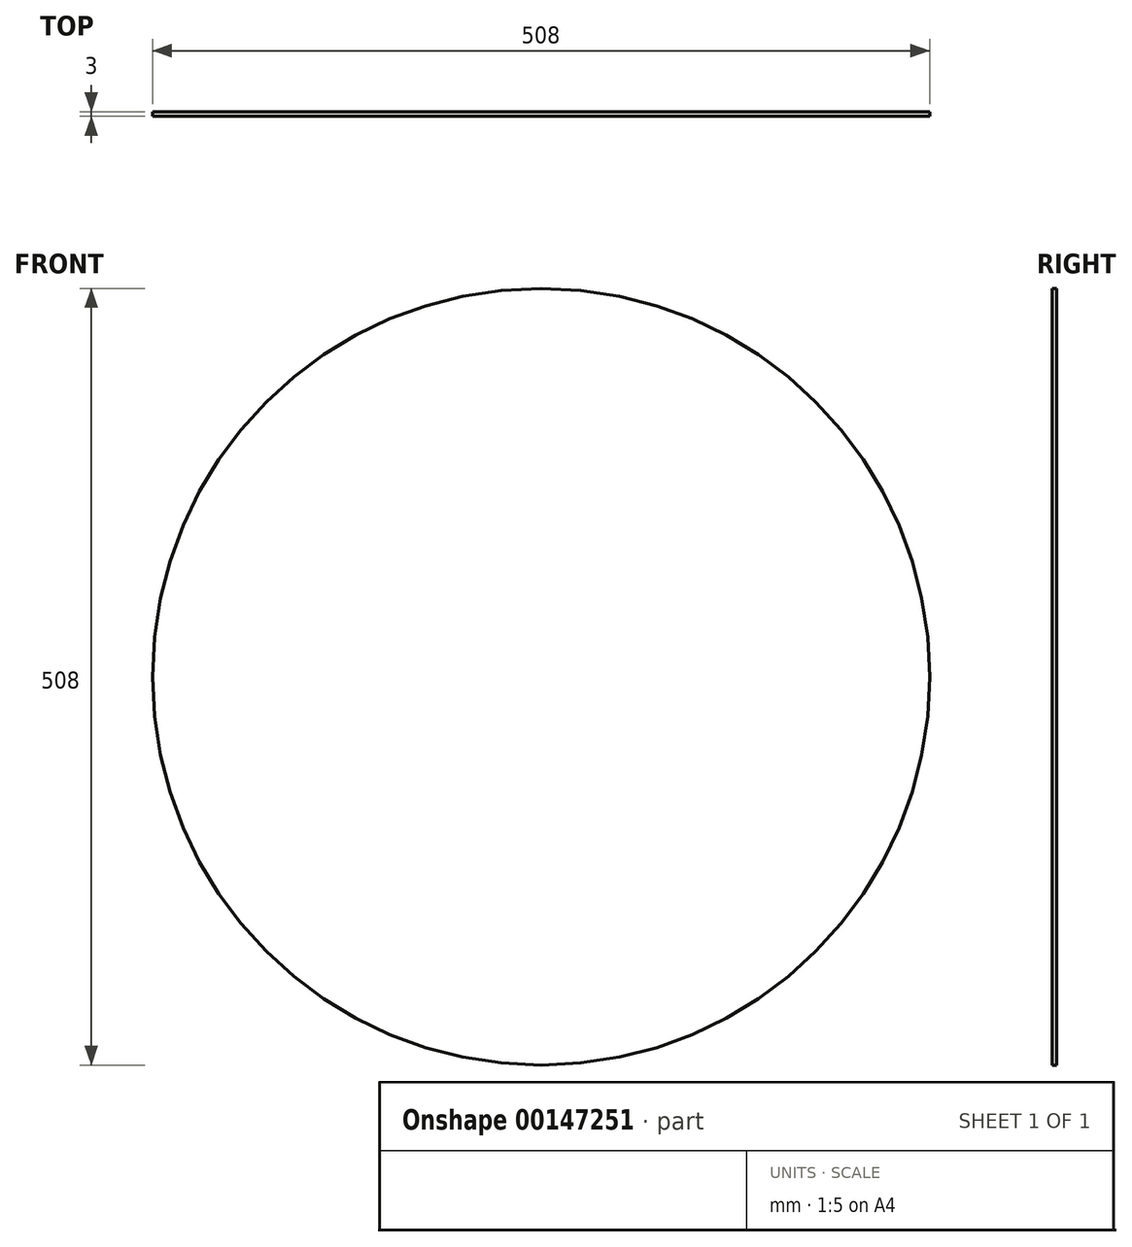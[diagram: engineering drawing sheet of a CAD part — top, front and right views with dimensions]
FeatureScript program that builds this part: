
annotation { "Feature Type Name" : "Feature", "Feature Type Description" : "" }
export const myFeature = defineFeature(function(context is Context, id is Id, definition is map)
    precondition{}
    {
        {
            var Q0;
            Q0=qCreatedBy(makeId("Front.planeOp"),FACE);
            var sketch = newSketch(context, id + "F0", { "sketchPlane" : qUnion([Q0])});
            skCircle(sketch, "E0", {"center": v(-25.18, 5.81) * mm, "radius": 254 * mm});
            skSolve(sketch);
        }
        {
            var Q0;
            Q0=makeQuery(id+"F0.imprint","IMPRINT",FACE,{"disambiguationData":[TD([[makeQuery(id+"F0.imprint","IMPRINT",EDGE,{"derivedFrom":sQuery(id+"F0.wireOp",EDGE,"E0")}),1.0]])]});
            extrude(context, id + "F1", {"entities" : qUnion([Q0]), "depth" : 3 * mm});
        }
    });
